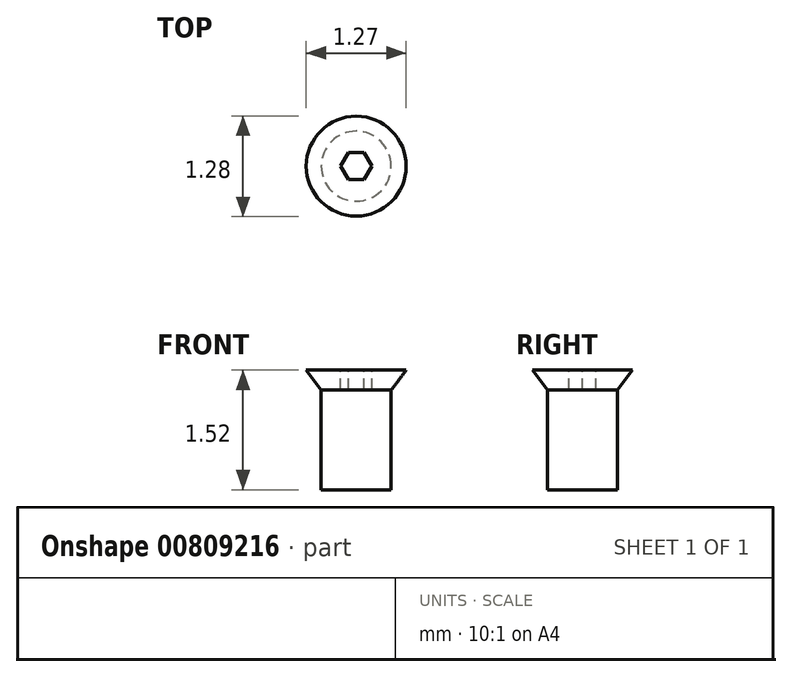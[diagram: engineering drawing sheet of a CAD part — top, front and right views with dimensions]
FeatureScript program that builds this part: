
annotation { "Feature Type Name" : "Feature", "Feature Type Description" : "" }
export const myFeature = defineFeature(function(context is Context, id is Id, definition is map)
    precondition{}
    {
        {
            var Q0;
            Q0=qCreatedBy(makeId("Front.planeOp"),FACE);
            var sketch = newSketch(context, id + "F0", { "sketchPlane" : qUnion([Q0])});
            skLineSegment(sketch, "E0", {"start": v(-45.87, 40.72) * mm, "end": v(-45.23, 40.72) * mm});
            skLineSegment(sketch, "E1", {"start": v(-45.68, 40.46) * mm, "end": v(-45.87, 40.72) * mm});
            skLineSegment(sketch, "E2", {"start": v(-45.23, 40.72) * mm, "end": v(-45.23, 39.2) * mm});
            skLineSegment(sketch, "E3", {"start": v(-45.23, 39.2) * mm, "end": v(-45.68, 39.2) * mm});
            skLineSegment(sketch, "E4", {"start": v(-45.68, 39.2) * mm, "end": v(-45.68, 40.46) * mm});
            skSolve(sketch);
        }
        {
            var Q0;
            Q0=makeQuery(id+"F0.imprint","IMPRINT",FACE,{"disambiguationData":[TD([[makeQuery(id+"F0.imprint","IMPRINT",EDGE,{"derivedFrom":sQuery(id+"F0.wireOp",EDGE,"qpcFVGmX-f2HJ-9Kyq-I9se-6seGqbrA94wZ")}),-1.0]])]});
            var Q1;
            Q1=makeQuery(id+"F0.imprint","IMPRINT",FACE,{"disambiguationData":[TD([[makeQuery(id+"F0.imprint","IMPRINT",EDGE,{"derivedFrom":sQuery(id+"F0.wireOp",EDGE,"E0")}),-1.0]])]});
            var Q2;
            Q2=sQuery(id+"F0.wireOp",EDGE,"E2");
            revolve(context, id + "F1", {"surfaceOperationType" : NewSurfaceOperationType.NEW, "entities" : qUnion([Q0, Q1]), "axis" : qUnion([Q2]), "revolveType" : RevolveType.FULL});
        }
        {
            var Q0;
            Q0=makeQuery(id+"F1.opRevolve","SWEPT_FACE",FACE,{"disambiguationData":[OSD([sQuery(id+"F0.wireOp",EDGE,"E0")])]});
            var sketch = newSketch(context, id + "F2", { "sketchPlane" : qUnion([Q0])});
            skCircle(sketch, "E5.cCircle", {"center": v(-45.23, 0) * mm, "radius": 0.17 * mm, "construction": true});
            skLineSegment(sketch, "E5.0", {"start": v(-45.33, 0.17) * mm, "end": v(-45.13, 0.17) * mm});
            skLineSegment(sketch, "E5.1", {"start": v(-45.13, 0.17) * mm, "end": v(-45.03, 0) * mm});
            skLineSegment(sketch, "E5.2", {"start": v(-45.03, 0) * mm, "end": v(-45.13, -0.17) * mm});
            skLineSegment(sketch, "E5.3", {"start": v(-45.13, -0.17) * mm, "end": v(-45.33, -0.17) * mm});
            skLineSegment(sketch, "E5.4", {"start": v(-45.33, -0.17) * mm, "end": v(-45.43, 0) * mm});
            skLineSegment(sketch, "E5.5", {"start": v(-45.43, 0) * mm, "end": v(-45.33, 0.17) * mm});
            skPoint(sketch, "E5.0.midPoint", {"position": v(-45.23, 0.17) * mm});
            skSolve(sketch);
        }
        {
            var Q0;
            Q0=makeQuery(id+"F2.imprint","IMPRINT",FACE,{"disambiguationData":[TD([[makeQuery(id+"F2.imprint","IMPRINT",EDGE,{"derivedFrom":sQuery(id+"F2.wireOp",EDGE,"E5.0")}),-1.0]])]});
            extrude(context, id + "F3", {"entities" : qUnion([Q0]), "operationType" : NewBodyOperationType.REMOVE, "oppositeDirection" : true, "depth" : 0.25 * mm, "offsetDistance" : 25.4 * mm});
        }
    });
